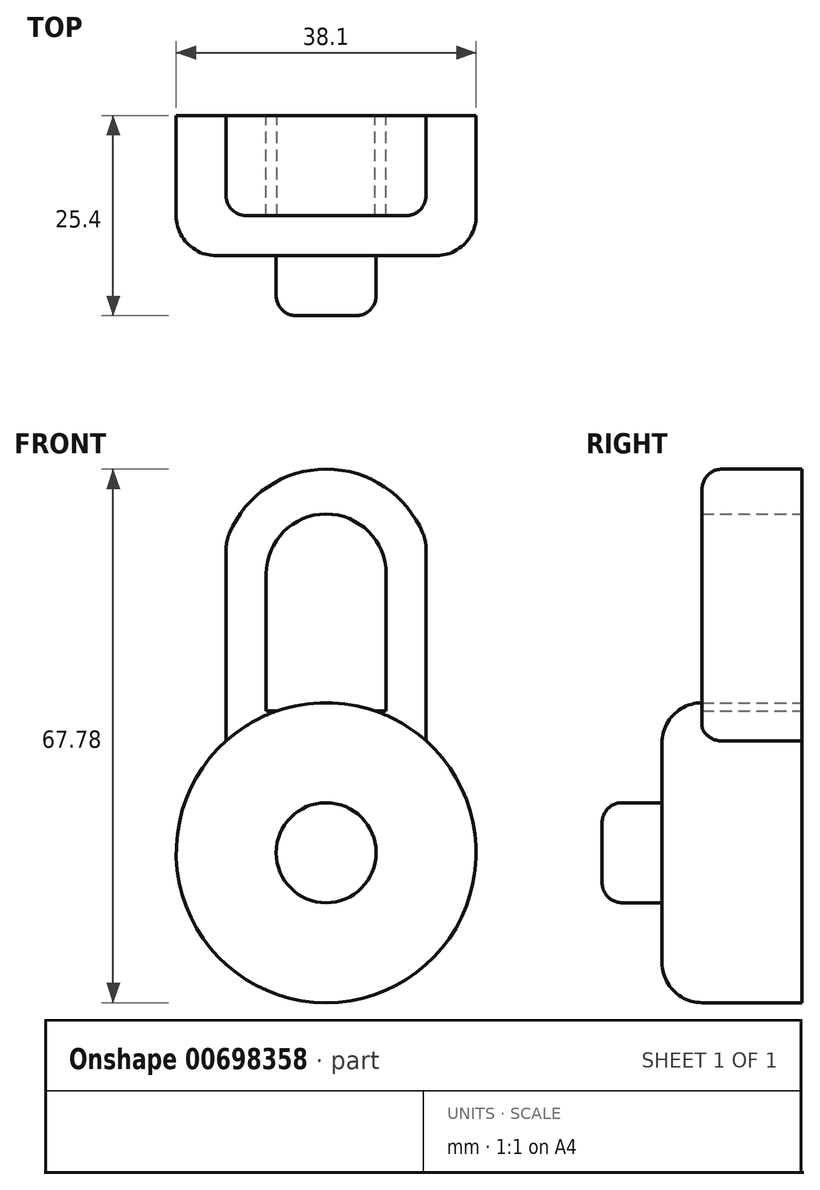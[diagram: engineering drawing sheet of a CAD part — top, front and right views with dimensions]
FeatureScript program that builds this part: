
annotation { "Feature Type Name" : "Feature", "Feature Type Description" : "" }
export const myFeature = defineFeature(function(context is Context, id is Id, definition is map)
    precondition{}
    {
        {
            var Q0;
            Q0=qCreatedBy(makeId("Front.planeOp"),FACE);
            var sketch = newSketch(context, id + "F0", { "sketchPlane" : qUnion([Q0])});
            skCircle(sketch, "E0", {"center": v(0, 0) * mm, "radius": 19.05 * mm});
            skSolve(sketch);
        }
        {
            var Q0;
            Q0=makeQuery(id+"F0.imprint","IMPRINT",FACE,{"disambiguationData":[TD([[makeQuery(id+"F0.imprint","IMPRINT",EDGE,{"derivedFrom":sQuery(id+"F0.wireOp",EDGE,"E0")}),1.0]])]});
            extrude(context, id + "F1", {"entities" : qUnion([Q0]), "depth" : 17.78 * mm, "offsetDistance" : 25.4 * mm});
        }
        {
            var Q0;
            Q0=makeQuery(id+"F1.opExtrude","CAP_EDGE",EDGE,{"disambiguationData":[OSD([sQuery(id+"F0.wireOp",EDGE,"E0")])],"isStart":false});
            fillet(context, id + "F2", {"entities" : qUnion([Q0]), "radius" : 5.08 * mm, "tangentPropagation" : true, "allowEdgeOverflow" : false});
        }
        {
            var Q0;
            Q0=makeQuery(id+"F1.opExtrude","CAP_FACE",FACE,{"disambiguationData":[OSD([sQuery(id+"F0.wireOp",EDGE,"E0")])],"isStart":false});
            var sketch = newSketch(context, id + "F3", { "sketchPlane" : qUnion([Q0])});
            skCircle(sketch, "E1", {"center": v(0, 0) * mm, "radius": 6.35 * mm});
            skSolve(sketch);
        }
        {
            var Q0;
            Q0=makeQuery(id+"F3.imprint","IMPRINT",FACE,{"disambiguationData":[TD([[makeQuery(id+"F3.imprint","IMPRINT",EDGE,{"derivedFrom":sQuery(id+"F3.wireOp",EDGE,"E1")}),1.0]])]});
            extrude(context, id + "F4", {"entities" : qUnion([Q0]), "operationType" : NewBodyOperationType.ADD, "depth" : 7.62 * mm, "offsetDistance" : 25.4 * mm});
        }
        {
            var Q0;
            Q0=makeQuery(id+"F4.opExtrude","CAP_EDGE",EDGE,{"disambiguationData":[OSD([sQuery(id+"F3.wireOp",EDGE,"E1")])],"isStart":false});
            fillet(context, id + "F5", {"entities" : qUnion([Q0]), "radius" : 2.54 * mm, "tangentPropagation" : true, "allowEdgeOverflow" : false});
        }
        {
            var Q0;
            Q0=qCreatedBy(makeId("Front.planeOp"),FACE);
            var sketch = newSketch(context, id + "F6", { "sketchPlane" : qUnion([Q0])});
            skArc(sketch, "E2", {"start": v(-12.7, 39.45) * mm, "mid": v(0, 48.73) * mm, "end": v(12.7, 39.45) * mm});
            skLineSegment(sketch, "E3", {"start": v(-12.7, 39.45) * mm, "end": v(-12.7, 13.89) * mm});
            skLineSegment(sketch, "E4", {"start": v(-12.7, 13.89) * mm, "end": v(12.7, 13.89) * mm});
            skLineSegment(sketch, "E5", {"start": v(12.7, 13.89) * mm, "end": v(12.7, 39.45) * mm});
            skArc(sketch, "E6", {"start": v(-7.62, 35.4) * mm, "mid": v(0, 43.02) * mm, "end": v(7.62, 35.4) * mm});
            skLineSegment(sketch, "E7", {"start": v(-7.62, 35.4) * mm, "end": v(-7.62, 18) * mm});
            skLineSegment(sketch, "E8", {"start": v(-7.62, 18) * mm, "end": v(7.62, 18) * mm});
            skLineSegment(sketch, "E9", {"start": v(7.62, 18) * mm, "end": v(7.62, 35.4) * mm});
            skSolve(sketch);
        }
        {
            var Q0;
            Q0 = qSketchRegion(id + "F6", true);
            extrude(context, id + "F7", {"entities" : qUnion([Q0]), "operationType" : NewBodyOperationType.ADD, "depth" : 12.7 * mm, "offsetDistance" : 25.4 * mm});
        }
        {
            var Q0;
            Q0=makeQuery(id+"F7.opExtrude","CAP_EDGE",EDGE,{"disambiguationData":[OSD([sQuery(id+"F6.wireOp",EDGE,"E3")])],"isStart":false});
            var Q1;
            Q1=makeQuery(id+"F7.opExtrude","CAP_EDGE",EDGE,{"disambiguationData":[OSD([sQuery(id+"F6.wireOp",EDGE,"E2")])],"isStart":false});
            var Q2;
            Q2=makeQuery(id+"F7.opExtrude","CAP_EDGE",EDGE,{"disambiguationData":[OSD([sQuery(id+"F6.wireOp",EDGE,"E5")])],"isStart":false});
            fillet(context, id + "F8", {"entities" : qUnion([Q0, Q1, Q2]), "radius" : 2.54 * mm, "tangentPropagation" : true, "allowEdgeOverflow" : false});
        }
        {
            var Q0;
            Q0=makeQuery(id+"F7.opExtrude","SWEPT_EDGE",EDGE,{"disambiguationData":[OSD([sQuery(id+"F6.wireOp",EDGE,"E2"),sQuery(id+"F6.wireOp",EDGE,"E3")])]});
            var Q1;
            Q1=makeQuery(id+"F7.opExtrude","SWEPT_EDGE",EDGE,{"disambiguationData":[OSD([sQuery(id+"F6.wireOp",EDGE,"E2"),sQuery(id+"F6.wireOp",EDGE,"E5")])]});
            fillet(context, id + "F9", {"entities" : qUnion([Q0, Q1]), "radius" : 5.08 * mm, "tangentPropagation" : true, "allowEdgeOverflow" : false});
        }
    });
